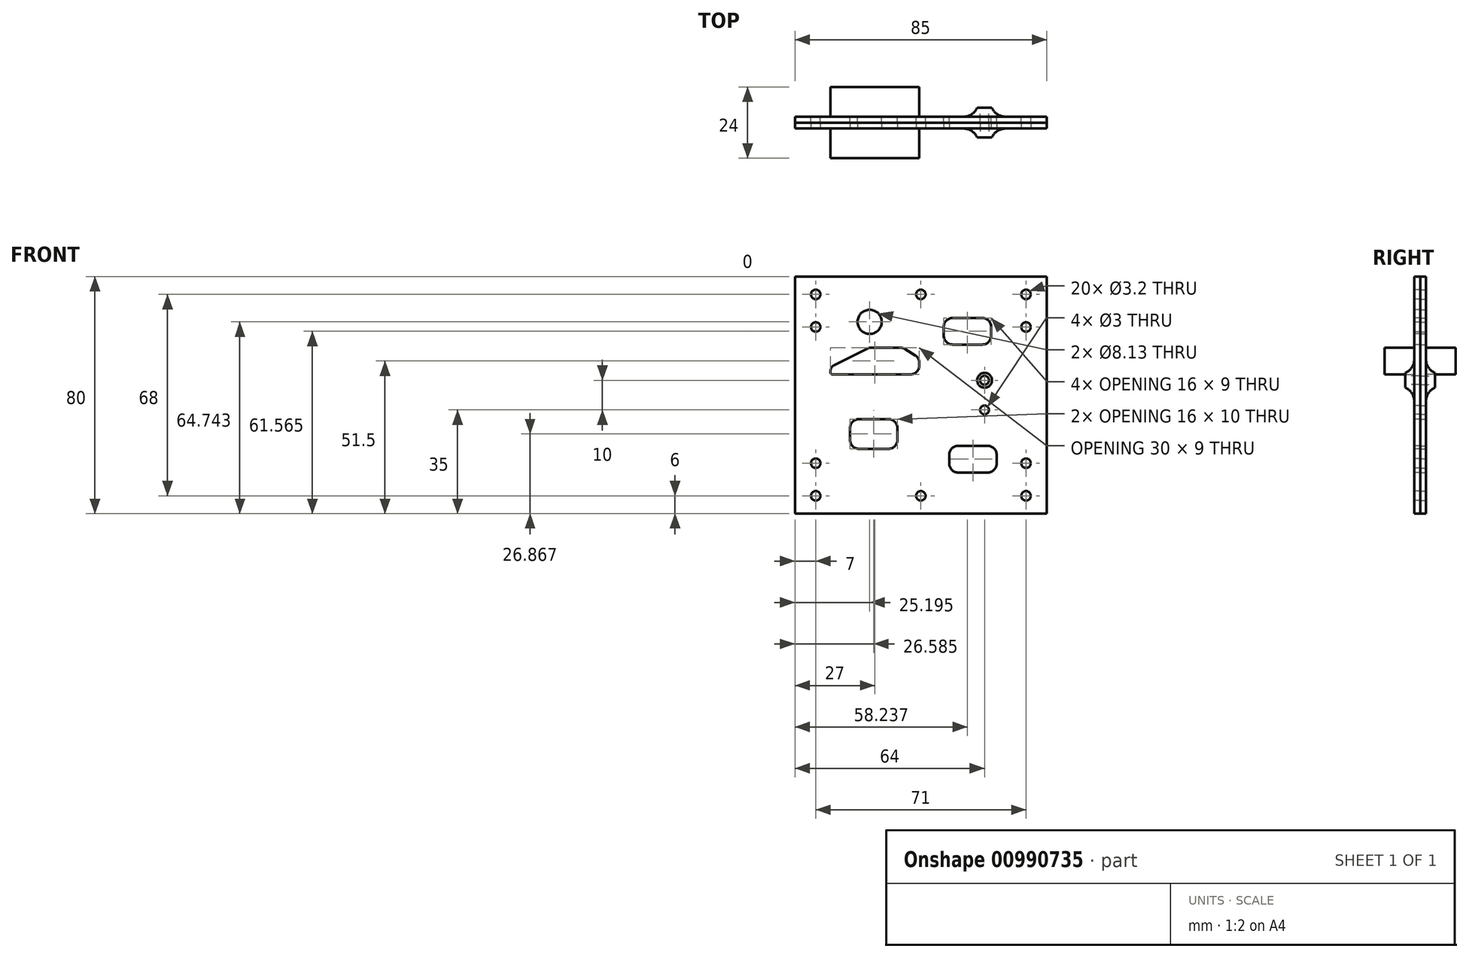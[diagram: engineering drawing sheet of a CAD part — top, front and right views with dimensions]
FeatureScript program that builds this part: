
annotation { "Feature Type Name" : "Feature", "Feature Type Description" : "" }
export const myFeature = defineFeature(function(context is Context, id is Id, definition is map)
    precondition{}
    {
        {
            var Q0;
            Q0=qCreatedBy(makeId("Front.planeOp"),FACE);
            var sketch = newSketch(context, id + "F0", { "sketchPlane" : qUnion([Q0])});
            skLineSegment(sketch, "E0.top", {"start": v(42.5, -4) * mm, "end": v(-42.5, -4) * mm, "construction": true});
            skLineSegment(sketch, "E0.left", {"start": v(42.5, 4) * mm, "end": v(42.5, -4) * mm});
            skLineSegment(sketch, "E0.right", {"start": v(-42.5, 4) * mm, "end": v(-42.5, -4) * mm});
            skPoint(sketch, "E0.middle", {"position": v(0, 0) * mm});
            skLineSegment(sketch, "E1.bottom", {"start": v(-42.5, 4) * mm, "end": v(42.5, 4) * mm, "construction": true});
            skLineSegment(sketch, "E1.top", {"start": v(-42.5, 6) * mm, "end": v(42.5, 6) * mm});
            skLineSegment(sketch, "E1.left", {"start": v(-42.5, 4) * mm, "end": v(-42.5, 6) * mm});
            skLineSegment(sketch, "E1.right", {"start": v(42.5, 4) * mm, "end": v(42.5, 6) * mm});
            skCircle(sketch, "E2", {"center": v(0, 0) * mm, "radius": 1.6 * mm});
            skCircle(sketch, "E3", {"center": v(35.5, 0) * mm, "radius": 1.6 * mm});
            skCircle(sketch, "E4", {"center": v(-35.5, 0) * mm, "radius": 1.6 * mm});
            skLineSegment(sketch, "E5.top", {"start": v(-42.5, -34) * mm, "end": v(42.5, -34) * mm});
            skLineSegment(sketch, "E5.left", {"start": v(-42.5, -4) * mm, "end": v(-42.5, -34) * mm});
            skLineSegment(sketch, "E5.right", {"start": v(42.5, -4) * mm, "end": v(42.5, -34) * mm});
            skCircle(sketch, "E6", {"center": v(-35.5, -11) * mm, "radius": 1.6 * mm});
            skCircle(sketch, "E7", {"center": v(35.5, -11) * mm, "radius": 1.6 * mm});
            skCircle(sketch, "E8", {"center": v(21.5, -29) * mm, "radius": 2.5 * mm});
            skLineSegment(sketch, "E9.bottom", {"start": v(-29.95, -27) * mm, "end": v(-3.5, -27) * mm});
            skCircle(sketch, "E10", {"center": v(-17.5, -36) * mm, "radius": 1.75 * mm, "construction": true});
            skCircle(sketch, "E11", {"center": v(21.5, -29) * mm, "radius": 1.5 * mm});
            skLineSegment(sketch, "E12", {"start": v(-0.5, -24) * mm, "end": v(-0.5, -23.15) * mm});
            skLineSegment(sketch, "E13", {"start": v(-1.89, -20.62) * mm, "end": v(-5.26, -18.47) * mm});
            skLineSegment(sketch, "E14", {"start": v(-6.87, -18) * mm, "end": v(-17.03, -18) * mm});
            skLineSegment(sketch, "E15", {"start": v(-30.5, -26.45) * mm, "end": v(-30.5, -25.74) * mm});
            skLineSegment(sketch, "E16", {"start": v(-29.4, -23.95) * mm, "end": v(-17.92, -18.21) * mm});
            skPoint(sketch, "E17.visualSharp", {"position": v(-0.5, -21.5) * mm});
            skArc(sketch, "E17.filletArc", {"start": v(-0.5, -23.15) * mm, "mid": v(-0.87, -21.7) * mm, "end": v(-1.89, -20.62) * mm});
            skPoint(sketch, "E18.visualSharp", {"position": v(-0.5, -27) * mm});
            skArc(sketch, "E18.filletArc", {"start": v(-3.5, -27) * mm, "mid": v(-1.38, -26.12) * mm, "end": v(-0.5, -24) * mm});
            skPoint(sketch, "E19.visualSharp", {"position": v(-6, -18) * mm});
            skArc(sketch, "E19.filletArc", {"start": v(-5.26, -18.47) * mm, "mid": v(-6.03, -18.12) * mm, "end": v(-6.87, -18) * mm});
            skPoint(sketch, "E20.visualSharp", {"position": v(-17.5, -18) * mm});
            skArc(sketch, "E20.filletArc", {"start": v(-17.03, -18) * mm, "mid": v(-17.49, -18.05) * mm, "end": v(-17.92, -18.21) * mm});
            skPoint(sketch, "E21.visualSharp", {"position": v(-30.5, -24.5) * mm});
            skArc(sketch, "E21.filletArc", {"start": v(-29.4, -23.95) * mm, "mid": v(-30.2, -24.68) * mm, "end": v(-30.5, -25.74) * mm});
            skPoint(sketch, "E22.visualSharp", {"position": v(-30.5, -27) * mm});
            skArc(sketch, "E22.filletArc", {"start": v(-30.5, -26.45) * mm, "mid": v(-30.34, -26.84) * mm, "end": v(-29.95, -27) * mm});
            skSolve(sketch);
        }
        {
            var Q0;
            Q0=makeQuery(id+"F0.imprint","IMPRINT",FACE,{"disambiguationData":[TD([[makeQuery(id+"F0.imprint","IMPRINT",EDGE,{"derivedFrom":sQuery(id+"F0.wireOp",EDGE,"E0.left")}),-1.0]])]});
            var Q1;
            Q1=makeQuery(id+"F0.imprint","IMPRINT",FACE,{"disambiguationData":[TD([[makeQuery(id+"F0.imprint","IMPRINT",EDGE,{"derivedFrom":sQuery(id+"F0.wireOp",EDGE,"E9.bottom")}),1.0]])]});
            var Q2;
            Q2=makeQuery(id+"F0.imprint","IMPRINT",FACE,{"disambiguationData":[TD([[makeQuery(id+"F0.imprint","IMPRINT",EDGE,{"derivedFrom":sQuery(id+"F0.wireOp",EDGE,"E8")}),1.0]])]});
            extrude(context, id + "F1", {"entities" : qUnion([Q0, Q1, Q2]), "oppositeDirection" : true, "depth" : 2 * mm, "offsetDistance" : 25 * mm});
        }
        {
            var Q0;
            Q0=makeQuery(id+"F1.opExtrude","SWEPT_BODY",BODY,{"disambiguationData":[OSD([sQuery(id+"F0.wireOp",EDGE,"E0.left"),sQuery(id+"F0.wireOp",EDGE,"E0.right"),sQuery(id+"F0.wireOp",EDGE,"E1.top"),sQuery(id+"F0.wireOp",EDGE,"E1.left"),sQuery(id+"F0.wireOp",EDGE,"E1.right"),sQuery(id+"F0.wireOp",EDGE,"E2"),sQuery(id+"F0.wireOp",EDGE,"E3"),sQuery(id+"F0.wireOp",EDGE,"E4"),sQuery(id+"F0.wireOp",EDGE,"E5.top"),sQuery(id+"F0.wireOp",EDGE,"E5.left"),sQuery(id+"F0.wireOp",EDGE,"E5.right"),sQuery(id+"F0.wireOp",EDGE,"E6"),sQuery(id+"F0.wireOp",EDGE,"E7"),sQuery(id+"F0.wireOp",EDGE,"E11")])]});
            var Q1;
            Q1=makeQuery(id+"F1.opExtrude","SWEPT_FACE",FACE,{"disambiguationData":[OSD([sQuery(id+"F0.wireOp",EDGE,"E5.top")])]});
            mirror(context, id + "F2", {"operationType" : NewBodyOperationType.ADD, "entities" : qUnion([Q0]), "mirrorPlane" : qUnion([Q1])});
        }
        {
            var Q0;
            Q0=makeQuery(id+"F0.imprint","IMPRINT",FACE,{"disambiguationData":[TD([[makeQuery(id+"F0.imprint","IMPRINT",EDGE,{"derivedFrom":sQuery(id+"F0.wireOp",EDGE,"E9.bottom")}),1.0]])]});
            extrude(context, id + "F3", {"entities" : qUnion([Q0]), "operationType" : NewBodyOperationType.ADD, "depth" : 10 * mm, "offsetDistance" : 25 * mm});
        }
        {
            var Q0;
            Q0=makeQuery(id+"F0.imprint","IMPRINT",FACE,{"disambiguationData":[TD([[makeQuery(id+"F0.imprint","IMPRINT",EDGE,{"derivedFrom":sQuery(id+"F0.wireOp",EDGE,"E8")}),1.0]])]});
            extrude(context, id + "F4", {"entities" : qUnion([Q0]), "operationType" : NewBodyOperationType.ADD, "depth" : 3 * mm, "offsetDistance" : 25 * mm, "hasSecondDirection" : true, "secondDirectionOppositeDirection" : true, "secondDirectionDepth" : 2 * mm});
        }
        {
            var Q0;
            {var subQ0=makeQuery(id+"F1.opExtrude","CAP_FACE",FACE,{"disambiguationData":[OSD([sQuery(id+"F0.wireOp",EDGE,"E0.left"),sQuery(id+"F0.wireOp",EDGE,"E0.right"),sQuery(id+"F0.wireOp",EDGE,"E1.top"),sQuery(id+"F0.wireOp",EDGE,"E1.left"),sQuery(id+"F0.wireOp",EDGE,"E1.right"),sQuery(id+"F0.wireOp",EDGE,"E2"),sQuery(id+"F0.wireOp",EDGE,"E3"),sQuery(id+"F0.wireOp",EDGE,"E4"),sQuery(id+"F0.wireOp",EDGE,"E5.top"),sQuery(id+"F0.wireOp",EDGE,"E5.left"),sQuery(id+"F0.wireOp",EDGE,"E5.right"),sQuery(id+"F0.wireOp",EDGE,"E6"),sQuery(id+"F0.wireOp",EDGE,"E7"),sQuery(id+"F0.wireOp",EDGE,"E11")])],"isStart":true});Q0=makeQuery(id+"F4.boolean.opBoolean","INTERSECT",EDGE,{"derivedFrom":[makeQuery(id+"F2.boolean.opBoolean","MERGE",FACE,{"derivedFrom":[subQ0,makeQuery(id+"F2.opPattern","COPY",FACE,{"derivedFrom":subQ0,"instanceName":"1"})]}),makeQuery(id+"F4.opExtrude","SWEPT_FACE",FACE,{"disambiguationData":[OSD([sQuery(id+"F0.wireOp",EDGE,"E8")])]})]});}
            fillet(context, id + "F5", {"entities" : qUnion([Q0]), "radius" : 5 * mm, "tangentPropagation" : true, "allowEdgeOverflow" : false});
        }
        {
            var Q0;
            {var subQ0=makeQuery(id+"F1.opExtrude","CAP_FACE",FACE,{"disambiguationData":[OSD([sQuery(id+"F0.wireOp",EDGE,"E0.left"),sQuery(id+"F0.wireOp",EDGE,"E0.right"),sQuery(id+"F0.wireOp",EDGE,"E1.top"),sQuery(id+"F0.wireOp",EDGE,"E1.left"),sQuery(id+"F0.wireOp",EDGE,"E1.right"),sQuery(id+"F0.wireOp",EDGE,"E2"),sQuery(id+"F0.wireOp",EDGE,"E3"),sQuery(id+"F0.wireOp",EDGE,"E4"),sQuery(id+"F0.wireOp",EDGE,"E5.top"),sQuery(id+"F0.wireOp",EDGE,"E5.left"),sQuery(id+"F0.wireOp",EDGE,"E5.right"),sQuery(id+"F0.wireOp",EDGE,"E6"),sQuery(id+"F0.wireOp",EDGE,"E7"),sQuery(id+"F0.wireOp",EDGE,"E11")])],"isStart":true});Q0=makeQuery(id+"F2.boolean.opBoolean","MERGE",FACE,{"derivedFrom":[subQ0,makeQuery(id+"F2.opPattern","COPY",FACE,{"derivedFrom":subQ0,"instanceName":"1"})]});}
            var sketch = newSketch(context, id + "F6", { "sketchPlane" : qUnion([Q0])});
            skLineSegment(sketch, "E23.bottom", {"start": v(12.58, -51.13) * mm, "end": v(22.58, -51.13) * mm});
            skLineSegment(sketch, "E23.top", {"start": v(12.58, -60.13) * mm, "end": v(22.58, -60.13) * mm});
            skLineSegment(sketch, "E23.left", {"start": v(9.58, -54.13) * mm, "end": v(9.58, -57.13) * mm});
            skLineSegment(sketch, "E23.right", {"start": v(25.58, -54.13) * mm, "end": v(25.58, -57.13) * mm});
            skPoint(sketch, "E24.visualSharp", {"position": v(9.58, -60.13) * mm});
            skArc(sketch, "E24.filletArc", {"start": v(9.58, -57.13) * mm, "mid": v(10.46, -59.26) * mm, "end": v(12.58, -60.13) * mm});
            skPoint(sketch, "E25.visualSharp", {"position": v(9.58, -51.13) * mm});
            skArc(sketch, "E25.filletArc", {"start": v(12.58, -51.13) * mm, "mid": v(10.46, -52.01) * mm, "end": v(9.58, -54.13) * mm});
            skPoint(sketch, "E26.visualSharp", {"position": v(25.58, -51.13) * mm});
            skArc(sketch, "E26.filletArc", {"start": v(25.58, -54.13) * mm, "mid": v(24.7, -52.01) * mm, "end": v(22.58, -51.13) * mm});
            skPoint(sketch, "E27.visualSharp", {"position": v(25.58, -60.13) * mm});
            skArc(sketch, "E27.filletArc", {"start": v(22.58, -60.13) * mm, "mid": v(24.7, -59.26) * mm, "end": v(25.58, -57.13) * mm});
            skLineSegment(sketch, "E28.bottom", {"start": v(-20.91, -42.13) * mm, "end": v(-10.91, -42.13) * mm});
            skLineSegment(sketch, "E28.top", {"start": v(-20.91, -52.13) * mm, "end": v(-10.91, -52.13) * mm});
            skLineSegment(sketch, "E28.left", {"start": v(-23.91, -45.13) * mm, "end": v(-23.91, -49.13) * mm});
            skLineSegment(sketch, "E28.right", {"start": v(-7.91, -45.13) * mm, "end": v(-7.91, -49.13) * mm});
            skPoint(sketch, "E29.visualSharp", {"position": v(-23.91, -52.13) * mm});
            skArc(sketch, "E29.filletArc", {"start": v(-23.91, -49.13) * mm, "mid": v(-23.04, -51.25) * mm, "end": v(-20.91, -52.13) * mm});
            skPoint(sketch, "E30.visualSharp", {"position": v(-23.91, -42.13) * mm});
            skArc(sketch, "E30.filletArc", {"start": v(-20.91, -42.13) * mm, "mid": v(-23.04, -43.01) * mm, "end": v(-23.91, -45.13) * mm});
            skPoint(sketch, "E31.visualSharp", {"position": v(-7.91, -42.13) * mm});
            skArc(sketch, "E31.filletArc", {"start": v(-7.91, -45.13) * mm, "mid": v(-8.8, -43.01) * mm, "end": v(-10.91, -42.13) * mm});
            skPoint(sketch, "E32.visualSharp", {"position": v(-7.91, -52.13) * mm});
            skArc(sketch, "E32.filletArc", {"start": v(-10.91, -52.13) * mm, "mid": v(-8.8, -51.25) * mm, "end": v(-7.91, -49.13) * mm});
            skLineSegment(sketch, "E33.bottom", {"start": v(10.74, -7.94) * mm, "end": v(20.74, -7.94) * mm});
            skLineSegment(sketch, "E33.top", {"start": v(10.74, -16.94) * mm, "end": v(20.74, -16.94) * mm});
            skLineSegment(sketch, "E33.left", {"start": v(7.74, -10.94) * mm, "end": v(7.74, -13.94) * mm});
            skLineSegment(sketch, "E33.right", {"start": v(23.74, -10.94) * mm, "end": v(23.74, -13.94) * mm});
            skPoint(sketch, "E34.visualSharp", {"position": v(7.74, -16.94) * mm});
            skArc(sketch, "E34.filletArc", {"start": v(7.74, -13.94) * mm, "mid": v(8.62, -16.06) * mm, "end": v(10.74, -16.94) * mm});
            skPoint(sketch, "E35.visualSharp", {"position": v(7.74, -7.94) * mm});
            skArc(sketch, "E35.filletArc", {"start": v(10.74, -7.94) * mm, "mid": v(8.62, -8.81) * mm, "end": v(7.74, -10.94) * mm});
            skPoint(sketch, "E36.visualSharp", {"position": v(23.74, -7.94) * mm});
            skArc(sketch, "E36.filletArc", {"start": v(23.74, -10.94) * mm, "mid": v(22.86, -8.81) * mm, "end": v(20.74, -7.94) * mm});
            skPoint(sketch, "E37.visualSharp", {"position": v(23.74, -16.94) * mm});
            skArc(sketch, "E37.filletArc", {"start": v(20.74, -16.94) * mm, "mid": v(22.86, -16.06) * mm, "end": v(23.74, -13.94) * mm});
            skCircle(sketch, "E38", {"center": v(-17.3, -9.26) * mm, "radius": 4.07 * mm});
            skSolve(sketch);
        }
        {
            var Q0;
            Q0=makeQuery(id+"F6.imprint","IMPRINT",FACE,{"disambiguationData":[TD([[makeQuery(id+"F6.imprint","IMPRINT",EDGE,{"derivedFrom":sQuery(id+"F6.wireOp",EDGE,"E23.bottom")}),-1.0]])]});
            var Q1;
            Q1=makeQuery(id+"F6.imprint","IMPRINT",FACE,{"disambiguationData":[TD([[makeQuery(id+"F6.imprint","IMPRINT",EDGE,{"derivedFrom":sQuery(id+"F6.wireOp",EDGE,"E28.bottom")}),-1.0]])]});
            var Q2;
            Q2=makeQuery(id+"F6.imprint","IMPRINT",FACE,{"disambiguationData":[TD([[makeQuery(id+"F6.imprint","IMPRINT",EDGE,{"derivedFrom":sQuery(id+"F6.wireOp",EDGE,"E33.bottom")}),-1.0]])]});
            var Q3;
            Q3=makeQuery(id+"F6.imprint","IMPRINT",FACE,{"disambiguationData":[TD([[makeQuery(id+"F6.imprint","IMPRINT",EDGE,{"derivedFrom":sQuery(id+"F6.wireOp",EDGE,"E38")}),1.0]])]});
            extrude(context, id + "F7", {"entities" : qUnion([Q0, Q1, Q2, Q3]), "operationType" : NewBodyOperationType.REMOVE, "oppositeDirection" : true, "depth" : 25 * mm, "offsetDistance" : 25 * mm});
        }
        {
            var Q0;
            Q0=makeQuery(id+"F1.opExtrude","SWEPT_BODY",BODY,{"disambiguationData":[OSD([sQuery(id+"F0.wireOp",EDGE,"E0.left"),sQuery(id+"F0.wireOp",EDGE,"E0.right"),sQuery(id+"F0.wireOp",EDGE,"E1.top"),sQuery(id+"F0.wireOp",EDGE,"E1.left"),sQuery(id+"F0.wireOp",EDGE,"E1.right"),sQuery(id+"F0.wireOp",EDGE,"E2"),sQuery(id+"F0.wireOp",EDGE,"E3"),sQuery(id+"F0.wireOp",EDGE,"E4"),sQuery(id+"F0.wireOp",EDGE,"E5.top"),sQuery(id+"F0.wireOp",EDGE,"E5.left"),sQuery(id+"F0.wireOp",EDGE,"E5.right"),sQuery(id+"F0.wireOp",EDGE,"E6"),sQuery(id+"F0.wireOp",EDGE,"E7"),sQuery(id+"F0.wireOp",EDGE,"E11")])]});
            var Q1;
            {var subQ0=makeQuery(id+"F1.opExtrude","CAP_FACE",FACE,{"disambiguationData":[OSD([sQuery(id+"F0.wireOp",EDGE,"E0.left"),sQuery(id+"F0.wireOp",EDGE,"E0.right"),sQuery(id+"F0.wireOp",EDGE,"E1.top"),sQuery(id+"F0.wireOp",EDGE,"E1.left"),sQuery(id+"F0.wireOp",EDGE,"E1.right"),sQuery(id+"F0.wireOp",EDGE,"E2"),sQuery(id+"F0.wireOp",EDGE,"E3"),sQuery(id+"F0.wireOp",EDGE,"E4"),sQuery(id+"F0.wireOp",EDGE,"E5.top"),sQuery(id+"F0.wireOp",EDGE,"E5.left"),sQuery(id+"F0.wireOp",EDGE,"E5.right"),sQuery(id+"F0.wireOp",EDGE,"E6"),sQuery(id+"F0.wireOp",EDGE,"E7"),sQuery(id+"F0.wireOp",EDGE,"E11")])],"isStart":false});Q1=makeQuery(id+"F2.boolean.opBoolean","MERGE",FACE,{"derivedFrom":[subQ0,makeQuery(id+"F2.opPattern","COPY",FACE,{"derivedFrom":subQ0,"instanceName":"1"})]});}
            mirror(context, id + "F8", {"entities" : qUnion([Q0]), "mirrorPlane" : qUnion([Q1])});
        }
    });
